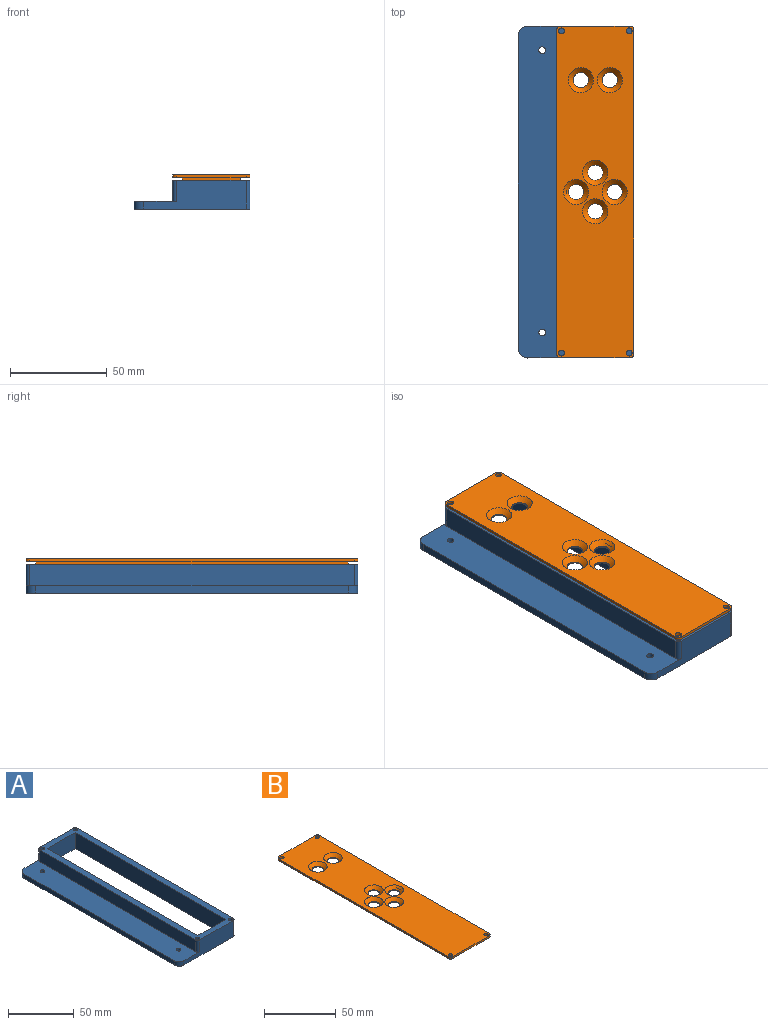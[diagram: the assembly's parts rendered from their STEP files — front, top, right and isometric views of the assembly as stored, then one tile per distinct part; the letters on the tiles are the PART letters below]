
ASSEMBLY  parts=2 mates=1
PART A: 28 faces, bbox 60x171.7x15 mm
  f0: plane 53x15mm, normal (0,1,0), area 608mm2, adj f4,f5,f7,f22,f25,f26
  f1: plane 161.7x4mm, normal (-1,0,0), area 646.8mm2, adj f4,f5,f26,f27
  f2: plane 53x15mm, normal (0,-1,0), area 608mm2, adj f4,f5,f7,f23,f24,f27
  f3: plane 167.7x15mm, normal (1,0,0), area 2515.5mm2, adj f5,f7,f24,f25
  f4: plane 171.7x22mm, normal (0,0,1), area 3405.7mm2, adj f0,f1,f2,f6,f8,f9,f22,f23
  f5: plane 171.7x60mm, normal (0,0,-1), area 5419.3mm2, adj f0,f1,f2,f3,f8,f9,f10,f11
  f6: plane 167.7x11mm, normal (-1,0,0), area 1844.7mm2, adj f4,f7,f22,f23
  f7: plane 171.7x40mm, normal (0,0,1), area 1985.3mm2, adj f0,f2,f3,f6,f10,f11,f12,f13
  f8: cylinder r=1.75mm len=4mm, axis (0,0,1), area 44mm2, adj f4,f5
  f9: cylinder r=1.75mm len=4mm, axis (0,0,1), area 44mm2, adj f4,f5
  f10: plane 161.7x15mm, normal (1,0,0), area 2425.5mm2, adj f5,f7,f11,f13
  f11: plane 30x15mm, normal (0,1,0), area 450mm2, adj f5,f7,f10,f12
  f12: plane 161.7x15mm, normal (-1,0,0), area 2425.5mm2, adj f5,f7,f11,f13
  f13: plane 30x15mm, normal (0,-1,0), area 450mm2, adj f5,f7,f10,f12
  f14: cylinder r=1.5mm len=9.5mm, axis (0,0,1), area 89.5mm2, adj f7,f15
  f15: plane 3x3mm, normal (0,0,1), area 7.1mm2, adj f14
  f16: cylinder r=1.5mm len=9.5mm, axis (0,0,1), area 89.5mm2, adj f7,f17
  f17: plane 3x3mm, normal (0,0,1), area 7.1mm2, adj f16
  f18: cylinder r=1.5mm len=9.5mm, axis (0,0,1), area 89.5mm2, adj f7,f19
  f19: plane 3x3mm, normal (0,0,1), area 7.1mm2, adj f18
  f20: cylinder r=1.5mm len=9.5mm, axis (0,0,1), area 89.5mm2, adj f7,f21
  f21: plane 3x3mm, normal (0,0,1), area 7.1mm2, adj f20
  f22: cylinder r=2mm len=11mm, axis (0,0,1), area 34.6mm2, adj f0,f4,f6,f7
  f23: cylinder r=2mm len=11mm, axis (0,0,-1), area 34.6mm2, adj f2,f4,f6,f7
  f24: cylinder r=2mm len=15mm, axis (0,0,1), area 47.1mm2, adj f2,f3,f5,f7
  f25: cylinder r=2mm len=15mm, axis (0,0,-1), area 47.1mm2, adj f0,f3,f5,f7
  f26: cylinder r=5mm len=5mm, axis (0,0,1), area 31.4mm2, adj f0,f1,f4,f5
  f27: cylinder r=5mm len=5mm, axis (0,0,-1), area 31.4mm2, adj f1,f2,f4,f5
PART B: 31 faces, bbox 40x171.7x3 mm
  f0: plane 171.7x40mm, normal (0,0,-1), area 1985.3mm2, adj f1,f2,f3,f4,f6,f7,f8,f9
  f1: plane 36x1.5mm, normal (0,1,0), area 54mm2, adj f0,f5,f19,f22
  f2: plane 167.7x1.5mm, normal (-1,0,0), area 251.5mm2, adj f0,f5,f19,f20
  f3: plane 36x1.5mm, normal (0,-1,0), area 54mm2, adj f0,f5,f20,f21
  f4: plane 167.7x1.5mm, normal (1,0,0), area 251.5mm2, adj f0,f5,f21,f22
  f5: plane 171.7x40mm, normal (0,0,1), area 6039.9mm2, adj f1,f2,f3,f4,f11,f12,f13,f14
  f6: plane 161.7x1.5mm, normal (-1,0,0), area 242.6mm2, adj f0,f7,f9,f10
  f7: plane 30x1.5mm, normal (0,1,0), area 45mm2, adj f0,f6,f8,f10
  f8: plane 161.7x1.5mm, normal (1,0,0), area 242.6mm2, adj f0,f7,f9,f10
  f9: plane 30x1.5mm, normal (0,-1,0), area 45mm2, adj f0,f6,f8,f10
  f10: plane 161.7x30mm, normal (0,0,-1), area 4549.4mm2, adj f6,f7,f8,f9,f15,f16,f17,f18
  f11: cylinder r=1.5mm len=3mm, axis (0,0,1), area 14.1mm2, adj f0,f5
  f12: cylinder r=1.5mm len=3mm, axis (0,0,1), area 14.1mm2, adj f0,f5
  f13: cylinder r=1.5mm len=3mm, axis (0,0,1), area 14.1mm2, adj f0,f5
  f14: cylinder r=1.5mm len=3mm, axis (0,0,1), area 14.1mm2, adj f0,f5
  f15: cylinder r=4mm len=8mm, axis (0,0,1), area 12.6mm2, adj f10,f23
  f16: cylinder r=4mm len=8mm, axis (0,0,1), area 12.6mm2, adj f10,f24
  f17: cylinder r=4mm len=8mm, axis (0,0,1), area 12.6mm2, adj f10,f25
  f18: cylinder r=4mm len=8mm, axis (0,0,1), area 12.6mm2, adj f10,f26
  f19: cylinder r=2mm len=2mm, axis (0,0,1), area 4.7mm2, adj f0,f1,f2,f5
  f20: cylinder r=2mm len=2mm, axis (0,0,-1), area 4.7mm2, adj f0,f2,f3,f5
  f21: cylinder r=2mm len=2mm, axis (0,0,1), area 4.7mm2, adj f0,f3,f4,f5
  f22: cylinder r=2mm len=2mm, axis (0,0,-1), area 4.7mm2, adj f0,f1,f4,f5
  f23: cone r=4mm half-angle=45deg, axis (0,0,1), area 116.6mm2, adj f5,f15
  f24: cone r=4mm half-angle=45deg, axis (0,0,1), area 116.6mm2, adj f5,f16
  f25: cone r=4mm half-angle=45deg, axis (0,0,1), area 116.6mm2, adj f5,f17
  f26: cone r=4mm half-angle=45deg, axis (0,0,1), area 116.6mm2, adj f5,f18
  f27: cylinder r=4mm len=8mm, axis (0,0,1), area 12.6mm2, adj f10,f29
  f28: cylinder r=4mm len=8mm, axis (0,0,1), area 12.6mm2, adj f10,f30
  f29: cone r=4mm half-angle=45deg, axis (0,0,1), area 116.6mm2, adj f5,f27
  f30: cone r=4mm half-angle=45deg, axis (0,0,1), area 116.6mm2, adj f5,f28
PLACE A t=(-31.77,-12.79,-105.67)mm
PLACE B t=(-96.21,-13.42,-89.4)mm
MATE slider A.f16 <-> B.f12  axis (0,0,1) through (-58.71,-218.32,-90.67)mm
